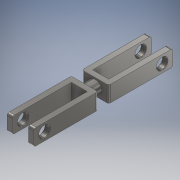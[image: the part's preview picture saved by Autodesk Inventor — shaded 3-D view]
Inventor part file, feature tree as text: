
AUTODESK INVENTOR PART (.ipt)
format: ipt  version: 2018 (Build 220112000, 112)  size: 192,512 bytes
history: native  units: mm
features: other x4, extrude x3, sketch x3, mirror x2, fillet x1, chamfer x1
ambient origin geometry x8: Origin, YZ Plane, XZ Plane, XY Plane, X Axis, Y Axis, Z Axis, Center Point
bodies: Solido1 (feature_tree)
feature tree (14):
  other  "Forcella movimento lama"
  extrude  "Estrusione1"  Depth=25.0mm
  extrude  "Estrusione2"  Depth=15.0mm
  fillet  "Raccordo1"  Radius=5.0mm
  extrude  "Estrusione3"  Depth=60.0mm
  other  "Mezzeria"
  mirror  "Specchio2"
  mirror  "Specchio3"
  chamfer  "Smusso1"  Distance=15.0mm
  sketch  "Schizzo1"
  sketch  "Schizzo2"
  other  "Linea chiusa proiettata1"
  sketch  "Schizzo3"
  other  "Linea chiusa proiettata2"
